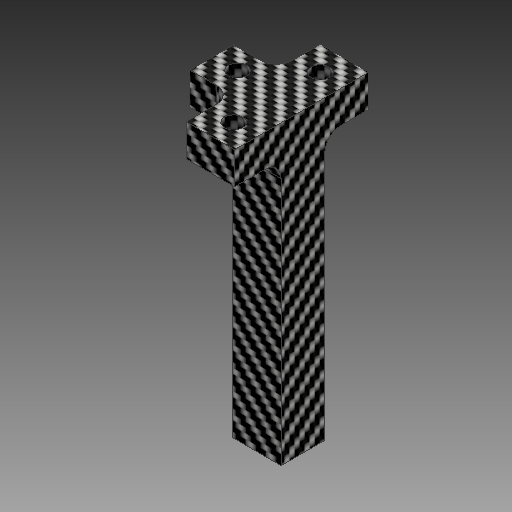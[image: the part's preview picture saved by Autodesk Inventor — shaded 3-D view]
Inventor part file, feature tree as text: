
AUTODESK INVENTOR PART (.ipt)
format: ipt  version: 2018 (Build 220112000, 112)  size: 242,176 bytes
history: native  units: mm
features: sketch x5, other x3
ambient origin geometry x8: Origin, YZ Plane, XZ Plane, XY Plane, X Axis, Y Axis, Z Axis, Center Point
bodies: Volumenkörper1 (feature_tree)
feature tree (8):
  other  "SolarpanelHalterung1.ipt"
  other  "Volumenkörper1::SolarpanelHalterung1.ipt"
  other  "Bezeichnung1"
  sketch  "Skizze1"  dims[d0=10.0mm]
  sketch  "Skizze2"
  sketch  "Skizze3"
  sketch  "Skizze4"
  sketch  "Skizze5"
